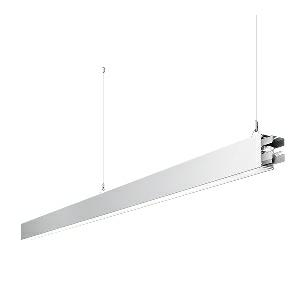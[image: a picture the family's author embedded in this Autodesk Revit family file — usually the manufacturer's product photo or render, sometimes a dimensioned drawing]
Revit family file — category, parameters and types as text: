
# Revit family: idoo_line_-_ilp_6000_830_d_mid_00805745_5479
name_source: partatom
category: Lighting Fixtures
units: mm (PartAtom-declared; Revit-internal decimal feet)

## family parameters
Cut with Voids When Loaded = No
Host = Face
Light Source = No
Part Type = Normal
Room Calculation Point = No
Round Connector Dimension = Use Diameter
Shared = No

## types (1)
- IDOO.line - ILP 6000/830/D MID (1 x LED, 6000 lm, 3000K)
    Apparent Load = 46 VA
    Approval mark = CE
    CIE Flux Codes = 66 91 98 40 100
    Color Rendering = 80-89
    Color Temperature = 3000K
    Control Gear = Electronic ballast
    Default Elevation = 1800 mm
    Description = ILP 6000/830/D|Suspended luminaire|light source: LED|connected load: 220-240 V, 50/60 Hz|Power consumption: approx. 46 W|standby: approx. 0,15|luminous flux: 6000 lm|luminous efficacy: 130 lm/W|light distribution: Direct/indirect|direct ratio: approx. 40 %|colour temperature: Warm white, ca. 3000 K|color rendering index (CRI): >= 80|chromaticity tolerance:  3 SDCM|System of protection: IP 40|technology: Continuously dimmable|luminaire body|material: Sectional aluminium|colour: White|lamp cover: Acrylic (PMMA), Clear|mains lead: 1,0 m With free stranded wires|Fastening: Steel cable 0.3 - 0.7 m|glare control: Prism aperture|luminance(L65): <= 2700 cd/m|unified glare rating(4H 8H): <=  16|special features: DALI Load 1x, TouchDIM - dimming via standard switch, Through-wired, up to 18 m on one mains connection, Flicker-free, Suitable as emergency lighting, Mechanical and electrical connection of the individual modules without tools|
    Frequency = 50 Hz
    Height = 110 mm
    Lamp = 1 x LED
    Lamp Light Flux = 6000 lm
    Lamp count = 1
    Length = 2244 mm
    Luminous efficacy = 130 lm/W
    Manufacturer = Waldmann
    ModVariant = No
    Model = 00805745
    Mounting Place = Ceiling
    Mounting Type = Pendant
    Number of Poles = 1
    OnlyDefault = Yes
    Power Factor = 1
    Product Name = IDOO.line - ILP 6000/830/D MID
    Product group = Suspended luminaire
    ProductGroupID = 9
    Protection Class = Protection class I
    Protection Degree = IP 40
    RLX_Detail_Level = 1
    RLX_Emergency_Light_Flux = 0 lm
    RLX_Emergency_Type = 0
    RLX_Emergency_Type_DB = No
    RlxData = <blob elided: 22093 chars, md5=2129a1e5>
    Socket = socket
    Standby Power = 0 W
    System Light Flux = 6000 lm
    System Power = 46 W
    Type Comments = Product without accessories
    Type Image = 113314000-00692606.jpg
    URL = http://relux.com
    VarID = ---
    Voltage = 230 V
    Voltage Range = 220-240 V
    Weight = 0.00 kg
    Width = 60 mm  [stored 0.19685 ft]

note: [stored X ft] marks values corroborated as IEEE doubles in the binary element streams (Revit-internal decimal feet)

## geometry (parser evidence)
native form markers: Blend x4, Sweep x13
no freeform markers — native parametric forms only
